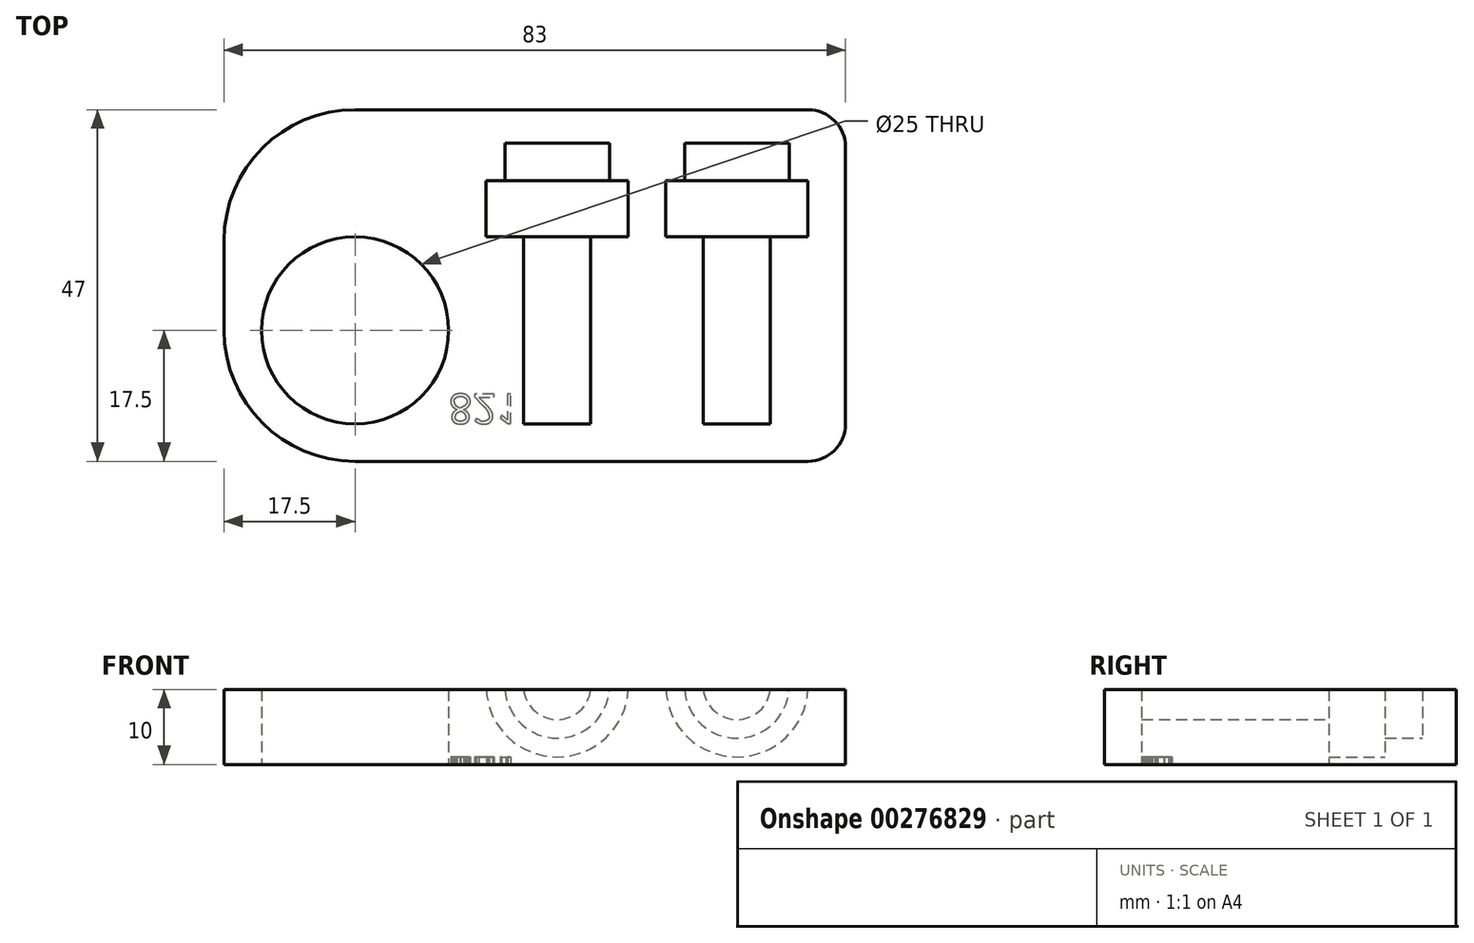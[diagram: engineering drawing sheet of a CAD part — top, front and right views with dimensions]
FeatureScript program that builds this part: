
annotation { "Feature Type Name" : "Feature", "Feature Type Description" : "" }
export const myFeature = defineFeature(function(context is Context, id is Id, definition is map)
    precondition{}
    {
        {
            var Q0;
            Q0=qCreatedBy(makeId("Top.planeOp"),FACE);
            var sketch = newSketch(context, id + "F0", { "sketchPlane" : qUnion([Q0])});
            skLineSegment(sketch, "E0.bottom", {"start": v(17.5, 0) * mm, "end": v(78, 0) * mm});
            skLineSegment(sketch, "E0.top", {"start": v(17.5, 47) * mm, "end": v(78, 47) * mm});
            skLineSegment(sketch, "E0.left", {"start": v(0, 17.5) * mm, "end": v(0, 29.5) * mm});
            skLineSegment(sketch, "E0.right", {"start": v(83, 5) * mm, "end": v(83, 42) * mm});
            skLineSegment(sketch, "E1.bottom", {"start": v(0, 0) * mm, "end": v(17.5, 0) * mm, "construction": true});
            skLineSegment(sketch, "E1.top", {"start": v(0, 17.5) * mm, "end": v(17.5, 17.5) * mm, "construction": true});
            skLineSegment(sketch, "E1.left", {"start": v(0, 0) * mm, "end": v(0, 17.5) * mm, "construction": true});
            skLineSegment(sketch, "E1.right", {"start": v(17.5, 0) * mm, "end": v(17.5, 17.5) * mm, "construction": true});
            skCircle(sketch, "E2", {"center": v(17.5, 17.5) * mm, "radius": 12.5 * mm});
            skPoint(sketch, "E3.visualSharp", {"position": v(0, 0) * mm});
            skArc(sketch, "E3.filletArc", {"start": v(0, 17.5) * mm, "mid": v(5.13, 5.13) * mm, "end": v(17.5, 0) * mm});
            skPoint(sketch, "E4.visualSharp", {"position": v(0, 47) * mm});
            skArc(sketch, "E4.filletArc", {"start": v(17.5, 47) * mm, "mid": v(5.13, 41.87) * mm, "end": v(0, 29.5) * mm});
            skPoint(sketch, "E5.visualSharp", {"position": v(83, 47) * mm});
            skArc(sketch, "E5.filletArc", {"start": v(83, 42) * mm, "mid": v(81.54, 45.54) * mm, "end": v(78, 47) * mm});
            skPoint(sketch, "E6.visualSharp", {"position": v(83, 0) * mm});
            skArc(sketch, "E6.filletArc", {"start": v(78, 0) * mm, "mid": v(81.54, 1.46) * mm, "end": v(83, 5) * mm});
            skSolve(sketch);
        }
        {
            var Q0;
            Q0=makeQuery(id+"F0.imprint","IMPRINT",FACE,{"disambiguationData":[TD([[makeQuery(id+"F0.imprint","IMPRINT",EDGE,{"derivedFrom":sQuery(id+"F0.wireOp",EDGE,"E0.bottom")}),1.0]])]});
            extrude(context, id + "F1", {"entities" : qUnion([Q0]), "depth" : 10 * mm});
        }
        {
            var Q0;
            Q0=makeQuery(id+"F1.opExtrude","CAP_FACE",FACE,{"disambiguationData":[OSD([sQuery(id+"F0.wireOp",EDGE,"E0.bottom"),sQuery(id+"F0.wireOp",EDGE,"E0.top"),sQuery(id+"F0.wireOp",EDGE,"E0.right"),sQuery(id+"F0.wireOp",EDGE,"E2"),sQuery(id+"F0.wireOp",EDGE,"E3.filletArc"),sQuery(id+"F0.wireOp",EDGE,"E4.filletArc"),sQuery(id+"F0.wireOp",EDGE,"E5.filletArc"),sQuery(id+"F0.wireOp",EDGE,"E6.filletArc")])],"isStart":false});
            cPlane(context, id + "F2", {"entities" : qUnion([Q0]), "cplaneType" : CPlaneType.OFFSET, "offset" : .5 * mm, "width" : 150 * mm, "height" : 150 * mm});
        }
        {
            var Q0;
            Q0=qCreatedBy(id+"F2.planeOp",FACE);
            var sketch = newSketch(context, id + "F3", { "sketchPlane" : qUnion([Q0])});
            skLineSegment(sketch, "E7.bottom", {"start": v(0, 0) * mm, "end": v(44.5, 0) * mm, "construction": true});
            skLineSegment(sketch, "E7.top", {"start": v(0, 5) * mm, "end": v(44.5, 5) * mm, "construction": true});
            skLineSegment(sketch, "E7.left", {"start": v(0, 0) * mm, "end": v(0, 5) * mm, "construction": true});
            skLineSegment(sketch, "E7.right", {"start": v(44.5, 0) * mm, "end": v(44.5, 5) * mm, "construction": true});
            skLineSegment(sketch, "E8", {"start": v(44.5, 5) * mm, "end": v(68.5, 5) * mm, "construction": true});
            skLineSegment(sketch, "E9.bottom", {"start": v(44.5, 5) * mm, "end": v(49, 5) * mm});
            skLineSegment(sketch, "E9.left", {"start": v(44.5, 5) * mm, "end": v(44.5, 30) * mm});
            skLineSegment(sketch, "E9.right", {"start": v(49, 5) * mm, "end": v(49, 30) * mm});
            skLineSegment(sketch, "E10.bottom", {"start": v(49, 30) * mm, "end": v(54, 30) * mm});
            skLineSegment(sketch, "E10.top", {"start": v(51.5, 37.5) * mm, "end": v(54, 37.5) * mm});
            skLineSegment(sketch, "E10.left", {"start": v(44.5, 30) * mm, "end": v(44.5, 37.5) * mm});
            skLineSegment(sketch, "E10.right", {"start": v(54, 30) * mm, "end": v(54, 37.5) * mm});
            skLineSegment(sketch, "E11.top", {"start": v(44.5, 42.5) * mm, "end": v(51.5, 42.5) * mm});
            skLineSegment(sketch, "E11.left", {"start": v(44.5, 37.5) * mm, "end": v(44.5, 42.5) * mm});
            skLineSegment(sketch, "E11.right", {"start": v(51.5, 37.5) * mm, "end": v(51.5, 42.5) * mm});
            skLineSegment(sketch, "E12.bottom", {"start": v(68.5, 5) * mm, "end": v(73, 5) * mm});
            skLineSegment(sketch, "E12.left", {"start": v(68.5, 5) * mm, "end": v(68.5, 30) * mm});
            skLineSegment(sketch, "E12.right", {"start": v(73, 5) * mm, "end": v(73, 30) * mm});
            skLineSegment(sketch, "E13.bottom", {"start": v(73, 30) * mm, "end": v(78, 30) * mm});
            skLineSegment(sketch, "E13.top", {"start": v(75.5, 37.5) * mm, "end": v(78, 37.5) * mm});
            skLineSegment(sketch, "E13.left", {"start": v(68.5, 30) * mm, "end": v(68.5, 37.5) * mm});
            skLineSegment(sketch, "E13.right", {"start": v(78, 30) * mm, "end": v(78, 37.5) * mm});
            skLineSegment(sketch, "E14.top", {"start": v(68.5, 42.5) * mm, "end": v(75.5, 42.5) * mm});
            skLineSegment(sketch, "E14.left", {"start": v(68.5, 37.5) * mm, "end": v(68.5, 42.5) * mm});
            skLineSegment(sketch, "E14.right", {"start": v(75.5, 37.5) * mm, "end": v(75.5, 42.5) * mm});
            skSolve(sketch);
        }
        {
            var Q0;
            Q0=makeQuery(id+"F3.imprint","IMPRINT",FACE,{"disambiguationData":[TD([[makeQuery(id+"F3.imprint","IMPRINT",EDGE,{"derivedFrom":sQuery(id+"F3.wireOp",EDGE,"E9.bottom")}),1.0]])]});
            var Q1;
            Q1=sQuery(id+"F3.wireOp",EDGE,"E9.left");
            revolve(context, id + "F4", {"operationType" : NewBodyOperationType.REMOVE, "entities" : qUnion([Q0]), "axis" : qUnion([Q1]), "revolveType" : RevolveType.FULL, "oppositeDirection" : true});
        }
        {
            var Q0;
            Q0=makeQuery(id+"F3.imprint","IMPRINT",FACE,{"disambiguationData":[TD([[makeQuery(id+"F3.imprint","IMPRINT",EDGE,{"derivedFrom":sQuery(id+"F3.wireOp",EDGE,"E12.bottom")}),1.0]])]});
            var Q1;
            Q1=sQuery(id+"F3.wireOp",EDGE,"E12.left");
            revolve(context, id + "F5", {"operationType" : NewBodyOperationType.REMOVE, "entities" : qUnion([Q0]), "axis" : qUnion([Q1]), "revolveType" : RevolveType.FULL, "oppositeDirection" : true});
        }
        {
            var Q0;
            Q0=makeQuery(id+"F1.opExtrude","CAP_FACE",FACE,{"disambiguationData":[OSD([sQuery(id+"F0.wireOp",EDGE,"E0.bottom"),sQuery(id+"F0.wireOp",EDGE,"E0.top"),sQuery(id+"F0.wireOp",EDGE,"E0.left"),sQuery(id+"F0.wireOp",EDGE,"E0.right"),sQuery(id+"F0.wireOp",EDGE,"E2"),sQuery(id+"F0.wireOp",EDGE,"E3.filletArc"),sQuery(id+"F0.wireOp",EDGE,"E4.filletArc"),sQuery(id+"F0.wireOp",EDGE,"E5.filletArc"),sQuery(id+"F0.wireOp",EDGE,"E6.filletArc")])],"isStart":true});
            var sketch = newSketch(context, id + "F6", { "sketchPlane" : qUnion([Q0])});
            skLineSegment(sketch, "E15.bottom", {"start": v(0, 0) * mm, "end": v(30, 0) * mm, "construction": true});
            skLineSegment(sketch, "E15.top", {"start": v(0, -5) * mm, "end": v(30, -5) * mm, "construction": true});
            skLineSegment(sketch, "E15.left", {"start": v(0, 0) * mm, "end": v(0, -5) * mm, "construction": true});
            skLineSegment(sketch, "E15.right", {"start": v(30, 0) * mm, "end": v(30, -5) * mm, "construction": true});
            skText(sketch, "E16", { "text": "821", "fontName": "OpenSans-Regular.ttf"});
            const initialGuessF6  = {"E16": [0.03, -0.009, 1, 0, 0.004]};
            skSetInitialGuess(sketch, initialGuessF6);
            skSolve(sketch);
        }
        {
            var Q0;
            Q0 = qSketchRegion(id + "F6", true);
            extrude(context, id + "F7", {"entities" : qUnion([Q0]), "operationType" : NewBodyOperationType.REMOVE, "oppositeDirection" : true, "depth" : 1 * mm});
        }
    });
